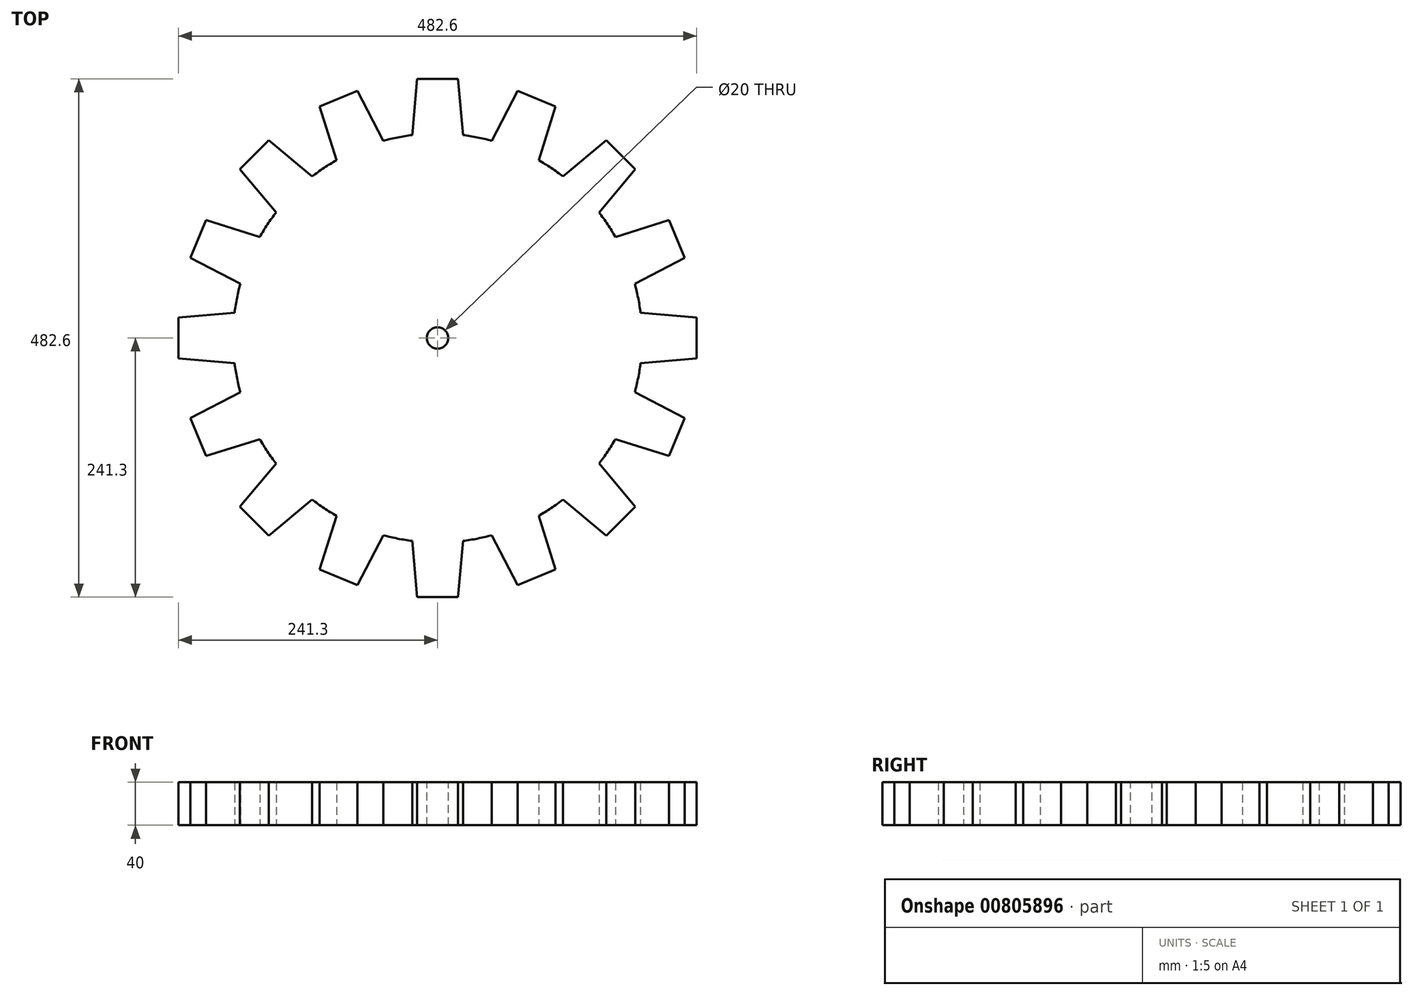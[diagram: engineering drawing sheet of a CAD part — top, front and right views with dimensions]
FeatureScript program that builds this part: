
annotation { "Feature Type Name" : "Feature", "Feature Type Description" : "" }
export const myFeature = defineFeature(function(context is Context, id is Id, definition is map)
    precondition{}
    {
        {
            var Q0;
            Q0=qCreatedBy(makeId("Top.planeOp"),FACE);
            var sketch = newSketch(context, id + "F0", { "sketchPlane" : qUnion([Q0])});
            skCircle(sketch, "E0", {"center": v(0, 0) * mm, "radius": 190.5 * mm});
            skLineSegment(sketch, "E1", {"start": v(0, 0) * mm, "end": v(0, 190.5) * mm, "construction": true});
            skLineSegment(sketch, "E2", {"start": v(-23.62, 189.03) * mm, "end": v(-19.05, 241.3) * mm});
            skLineSegment(sketch, "E3", {"start": v(-19.05, 241.3) * mm, "end": v(0, 241.3) * mm});
            skLineSegment(sketch, "E4.MirrorCS", {"start": v(23.62, 189.03) * mm, "end": v(19.05, 241.3) * mm});
            skLineSegment(sketch, "E5.MirrorCS", {"start": v(19.05, 241.3) * mm, "end": v(0, 241.3) * mm});
            skLineSegment(sketch, "E6.1.0", {"start": v(-94.16, 165.6) * mm, "end": v(-109.94, 215.64) * mm});
            skLineSegment(sketch, "E6.1.1", {"start": v(-109.94, 215.64) * mm, "end": v(-92.34, 222.93) * mm});
            skLineSegment(sketch, "E6.1.2", {"start": v(-74.74, 230.22) * mm, "end": v(-92.34, 222.93) * mm});
            skLineSegment(sketch, "E6.1.3", {"start": v(-50.51, 183.68) * mm, "end": v(-74.74, 230.22) * mm});
            skLineSegment(sketch, "E6.2.0", {"start": v(-150.37, 116.96) * mm, "end": v(-184.1, 157.15) * mm});
            skLineSegment(sketch, "E6.2.1", {"start": v(-184.1, 157.15) * mm, "end": v(-170.62, 170.62) * mm});
            skLineSegment(sketch, "E6.2.2", {"start": v(-157.15, 184.1) * mm, "end": v(-170.62, 170.62) * mm});
            skLineSegment(sketch, "E6.2.3", {"start": v(-116.96, 150.37) * mm, "end": v(-157.15, 184.1) * mm});
            skLineSegment(sketch, "E6.3.0", {"start": v(-183.68, 50.51) * mm, "end": v(-230.22, 74.74) * mm});
            skLineSegment(sketch, "E6.3.1", {"start": v(-230.22, 74.74) * mm, "end": v(-222.93, 92.34) * mm});
            skLineSegment(sketch, "E6.3.2", {"start": v(-215.64, 109.94) * mm, "end": v(-222.93, 92.34) * mm});
            skLineSegment(sketch, "E6.3.3", {"start": v(-165.6, 94.16) * mm, "end": v(-215.64, 109.94) * mm});
            skLineSegment(sketch, "E6.4.0", {"start": v(-189.03, -23.62) * mm, "end": v(-241.3, -19.05) * mm});
            skLineSegment(sketch, "E6.4.1", {"start": v(-241.3, -19.05) * mm, "end": v(-241.3, 0) * mm});
            skLineSegment(sketch, "E6.4.2", {"start": v(-241.3, 19.05) * mm, "end": v(-241.3, 0) * mm});
            skLineSegment(sketch, "E6.4.3", {"start": v(-189.03, 23.62) * mm, "end": v(-241.3, 19.05) * mm});
            skLineSegment(sketch, "E6.5.0", {"start": v(-165.6, -94.16) * mm, "end": v(-215.64, -109.94) * mm});
            skLineSegment(sketch, "E6.5.1", {"start": v(-215.64, -109.94) * mm, "end": v(-222.93, -92.34) * mm});
            skLineSegment(sketch, "E6.5.2", {"start": v(-230.22, -74.74) * mm, "end": v(-222.93, -92.34) * mm});
            skLineSegment(sketch, "E6.5.3", {"start": v(-183.68, -50.51) * mm, "end": v(-230.22, -74.74) * mm});
            skLineSegment(sketch, "E6.6.0", {"start": v(-116.96, -150.37) * mm, "end": v(-157.15, -184.1) * mm});
            skLineSegment(sketch, "E6.6.1", {"start": v(-157.15, -184.1) * mm, "end": v(-170.62, -170.62) * mm});
            skLineSegment(sketch, "E6.6.2", {"start": v(-184.1, -157.15) * mm, "end": v(-170.62, -170.62) * mm});
            skLineSegment(sketch, "E6.6.3", {"start": v(-150.37, -116.96) * mm, "end": v(-184.1, -157.15) * mm});
            skLineSegment(sketch, "E6.7.0", {"start": v(-50.51, -183.68) * mm, "end": v(-74.74, -230.22) * mm});
            skLineSegment(sketch, "E6.7.1", {"start": v(-74.74, -230.22) * mm, "end": v(-92.34, -222.93) * mm});
            skLineSegment(sketch, "E6.7.2", {"start": v(-109.94, -215.64) * mm, "end": v(-92.34, -222.93) * mm});
            skLineSegment(sketch, "E6.7.3", {"start": v(-94.16, -165.6) * mm, "end": v(-109.94, -215.64) * mm});
            skLineSegment(sketch, "E6.8.0", {"start": v(23.62, -189.03) * mm, "end": v(19.05, -241.3) * mm});
            skLineSegment(sketch, "E6.8.1", {"start": v(19.05, -241.3) * mm, "end": v(0, -241.3) * mm});
            skLineSegment(sketch, "E6.8.2", {"start": v(-19.05, -241.3) * mm, "end": v(0, -241.3) * mm});
            skLineSegment(sketch, "E6.8.3", {"start": v(-23.62, -189.03) * mm, "end": v(-19.05, -241.3) * mm});
            skLineSegment(sketch, "E6.9.0", {"start": v(94.16, -165.6) * mm, "end": v(109.94, -215.64) * mm});
            skLineSegment(sketch, "E6.9.1", {"start": v(109.94, -215.64) * mm, "end": v(92.34, -222.93) * mm});
            skLineSegment(sketch, "E6.9.2", {"start": v(74.74, -230.22) * mm, "end": v(92.34, -222.93) * mm});
            skLineSegment(sketch, "E6.9.3", {"start": v(50.51, -183.68) * mm, "end": v(74.74, -230.22) * mm});
            skLineSegment(sketch, "E6.10.0", {"start": v(150.37, -116.96) * mm, "end": v(184.1, -157.15) * mm});
            skLineSegment(sketch, "E6.10.1", {"start": v(184.1, -157.15) * mm, "end": v(170.62, -170.62) * mm});
            skLineSegment(sketch, "E6.10.2", {"start": v(157.15, -184.1) * mm, "end": v(170.62, -170.62) * mm});
            skLineSegment(sketch, "E6.10.3", {"start": v(116.96, -150.37) * mm, "end": v(157.15, -184.1) * mm});
            skLineSegment(sketch, "E6.11.0", {"start": v(183.68, -50.51) * mm, "end": v(230.22, -74.74) * mm});
            skLineSegment(sketch, "E6.11.1", {"start": v(230.22, -74.74) * mm, "end": v(222.93, -92.34) * mm});
            skLineSegment(sketch, "E6.11.2", {"start": v(215.64, -109.94) * mm, "end": v(222.93, -92.34) * mm});
            skLineSegment(sketch, "E6.11.3", {"start": v(165.6, -94.16) * mm, "end": v(215.64, -109.94) * mm});
            skLineSegment(sketch, "E6.12.0", {"start": v(189.03, 23.62) * mm, "end": v(241.3, 19.05) * mm});
            skLineSegment(sketch, "E6.12.1", {"start": v(241.3, 19.05) * mm, "end": v(241.3, 0) * mm});
            skLineSegment(sketch, "E6.12.2", {"start": v(241.3, -19.05) * mm, "end": v(241.3, 0) * mm});
            skLineSegment(sketch, "E6.12.3", {"start": v(189.03, -23.62) * mm, "end": v(241.3, -19.05) * mm});
            skLineSegment(sketch, "E6.13.0", {"start": v(165.6, 94.16) * mm, "end": v(215.64, 109.94) * mm});
            skLineSegment(sketch, "E6.13.1", {"start": v(215.64, 109.94) * mm, "end": v(222.93, 92.34) * mm});
            skLineSegment(sketch, "E6.13.2", {"start": v(230.22, 74.74) * mm, "end": v(222.93, 92.34) * mm});
            skLineSegment(sketch, "E6.13.3", {"start": v(183.68, 50.51) * mm, "end": v(230.22, 74.74) * mm});
            skLineSegment(sketch, "E6.14.0", {"start": v(116.96, 150.37) * mm, "end": v(157.15, 184.1) * mm});
            skLineSegment(sketch, "E6.14.1", {"start": v(157.15, 184.1) * mm, "end": v(170.62, 170.62) * mm});
            skLineSegment(sketch, "E6.14.2", {"start": v(184.1, 157.15) * mm, "end": v(170.62, 170.62) * mm});
            skLineSegment(sketch, "E6.14.3", {"start": v(150.37, 116.96) * mm, "end": v(184.1, 157.15) * mm});
            skLineSegment(sketch, "E6.15.0", {"start": v(50.51, 183.68) * mm, "end": v(74.74, 230.22) * mm});
            skLineSegment(sketch, "E6.15.1", {"start": v(74.74, 230.22) * mm, "end": v(92.34, 222.93) * mm});
            skLineSegment(sketch, "E6.15.2", {"start": v(109.94, 215.64) * mm, "end": v(92.34, 222.93) * mm});
            skLineSegment(sketch, "E6.15.3", {"start": v(94.16, 165.6) * mm, "end": v(109.94, 215.64) * mm});
            skSolve(sketch);
        }
        {
            var Q0;
            {var subQ0=sQuery(id+"F0.wireOp",EDGE,"E0");var subQ18=makeQuery(id+"F0.imprint","INTERSECT",VERTEX,{"derivedFrom":[subQ0,sQuery(id+"F0.wireOp",EDGE,"E6.12.0")]});Q0=makeQuery(id+"F0.imprint","IMPRINT",FACE,{"disambiguationData":[TD([[makeQuery(id+"F0.imprint","IMPRINT",EDGE,{"disambiguationData":[TD([[subQ18,-1.0]])],"derivedFrom":subQ0}),1.0]])]});}
            var Q1;
            Q1=qSketchRegion(id+"F0",true);
            extrude(context, id + "F1", {"entities" : qUnion([Q0, Q1]), "depth" : 20 * mm, "offsetDistance" : 25.4 * mm});
        }
        {
            var Q0;
            Q0=makeQuery(id+"F1.opExtrude","CAP_FACE",FACE,{"disambiguationData":[OSD([sQuery(id+"F0.wireOp",EDGE,"E0"),sQuery(id+"F0.wireOp",EDGE,"E2"),sQuery(id+"F0.wireOp",EDGE,"E3"),sQuery(id+"F0.wireOp",EDGE,"E4.MirrorCS"),sQuery(id+"F0.wireOp",EDGE,"E5.MirrorCS"),sQuery(id+"F0.wireOp",EDGE,"E6.1.0"),sQuery(id+"F0.wireOp",EDGE,"E6.1.1"),sQuery(id+"F0.wireOp",EDGE,"E6.1.2"),sQuery(id+"F0.wireOp",EDGE,"E6.1.3"),sQuery(id+"F0.wireOp",EDGE,"E6.2.0"),sQuery(id+"F0.wireOp",EDGE,"E6.2.1"),sQuery(id+"F0.wireOp",EDGE,"E6.2.2"),sQuery(id+"F0.wireOp",EDGE,"E6.2.3"),sQuery(id+"F0.wireOp",EDGE,"E6.3.0"),sQuery(id+"F0.wireOp",EDGE,"E6.3.1"),sQuery(id+"F0.wireOp",EDGE,"E6.3.2"),sQuery(id+"F0.wireOp",EDGE,"E6.3.3"),sQuery(id+"F0.wireOp",EDGE,"E6.4.0"),sQuery(id+"F0.wireOp",EDGE,"E6.4.1"),sQuery(id+"F0.wireOp",EDGE,"E6.4.2"),sQuery(id+"F0.wireOp",EDGE,"E6.4.3"),sQuery(id+"F0.wireOp",EDGE,"E6.5.0"),sQuery(id+"F0.wireOp",EDGE,"E6.5.1"),sQuery(id+"F0.wireOp",EDGE,"E6.5.2"),sQuery(id+"F0.wireOp",EDGE,"E6.5.3"),sQuery(id+"F0.wireOp",EDGE,"E6.6.0"),sQuery(id+"F0.wireOp",EDGE,"E6.6.1"),sQuery(id+"F0.wireOp",EDGE,"E6.6.2"),sQuery(id+"F0.wireOp",EDGE,"E6.6.3"),sQuery(id+"F0.wireOp",EDGE,"E6.7.0"),sQuery(id+"F0.wireOp",EDGE,"E6.7.1"),sQuery(id+"F0.wireOp",EDGE,"E6.7.2"),sQuery(id+"F0.wireOp",EDGE,"E6.7.3"),sQuery(id+"F0.wireOp",EDGE,"E6.8.0"),sQuery(id+"F0.wireOp",EDGE,"E6.8.1"),sQuery(id+"F0.wireOp",EDGE,"E6.8.2"),sQuery(id+"F0.wireOp",EDGE,"E6.8.3"),sQuery(id+"F0.wireOp",EDGE,"E6.9.0"),sQuery(id+"F0.wireOp",EDGE,"E6.9.1"),sQuery(id+"F0.wireOp",EDGE,"E6.9.2"),sQuery(id+"F0.wireOp",EDGE,"E6.9.3"),sQuery(id+"F0.wireOp",EDGE,"E6.10.0"),sQuery(id+"F0.wireOp",EDGE,"E6.10.1"),sQuery(id+"F0.wireOp",EDGE,"E6.10.2"),sQuery(id+"F0.wireOp",EDGE,"E6.10.3"),sQuery(id+"F0.wireOp",EDGE,"E6.11.0"),sQuery(id+"F0.wireOp",EDGE,"E6.11.1"),sQuery(id+"F0.wireOp",EDGE,"E6.11.2"),sQuery(id+"F0.wireOp",EDGE,"E6.11.3"),sQuery(id+"F0.wireOp",EDGE,"E6.12.0"),sQuery(id+"F0.wireOp",EDGE,"E6.12.1"),sQuery(id+"F0.wireOp",EDGE,"E6.12.2"),sQuery(id+"F0.wireOp",EDGE,"E6.12.3"),sQuery(id+"F0.wireOp",EDGE,"E6.13.0"),sQuery(id+"F0.wireOp",EDGE,"E6.13.1"),sQuery(id+"F0.wireOp",EDGE,"E6.13.2"),sQuery(id+"F0.wireOp",EDGE,"E6.13.3"),sQuery(id+"F0.wireOp",EDGE,"E6.14.0"),sQuery(id+"F0.wireOp",EDGE,"E6.14.1"),sQuery(id+"F0.wireOp",EDGE,"E6.14.2"),sQuery(id+"F0.wireOp",EDGE,"E6.14.3"),sQuery(id+"F0.wireOp",EDGE,"E6.15.0"),sQuery(id+"F0.wireOp",EDGE,"E6.15.1"),sQuery(id+"F0.wireOp",EDGE,"E6.15.2"),sQuery(id+"F0.wireOp",EDGE,"E6.15.3")])],"isStart":false});
            var sketch = newSketch(context, id + "F2", { "sketchPlane" : qUnion([Q0])});
            skCircle(sketch, "E7", {"center": v(0, 0) * mm, "radius": 10 * mm});
            skSolve(sketch);
        }
        {
            var Q0;
            Q0=qSketchRegion(id+"F2",true);
            extrude(context, id + "F3", {"entities" : qUnion([Q0]), "operationType" : NewBodyOperationType.REMOVE, "endBound" : BoundingType.THROUGH_ALL, "oppositeDirection" : true, "depth" : 25 * mm, "offsetDistance" : 25 * mm});
        }
        {
            var Q0;
            Q0=makeQuery(id+"F1.opExtrude","CAP_FACE",FACE,{"disambiguationData":[OSD([sQuery(id+"F0.wireOp",EDGE,"E0"),sQuery(id+"F0.wireOp",EDGE,"E2"),sQuery(id+"F0.wireOp",EDGE,"E3"),sQuery(id+"F0.wireOp",EDGE,"E4.MirrorCS"),sQuery(id+"F0.wireOp",EDGE,"E5.MirrorCS"),sQuery(id+"F0.wireOp",EDGE,"E6.1.0"),sQuery(id+"F0.wireOp",EDGE,"E6.1.1"),sQuery(id+"F0.wireOp",EDGE,"E6.1.2"),sQuery(id+"F0.wireOp",EDGE,"E6.1.3"),sQuery(id+"F0.wireOp",EDGE,"E6.2.0"),sQuery(id+"F0.wireOp",EDGE,"E6.2.1"),sQuery(id+"F0.wireOp",EDGE,"E6.2.2"),sQuery(id+"F0.wireOp",EDGE,"E6.2.3"),sQuery(id+"F0.wireOp",EDGE,"E6.3.0"),sQuery(id+"F0.wireOp",EDGE,"E6.3.1"),sQuery(id+"F0.wireOp",EDGE,"E6.3.2"),sQuery(id+"F0.wireOp",EDGE,"E6.3.3"),sQuery(id+"F0.wireOp",EDGE,"E6.4.0"),sQuery(id+"F0.wireOp",EDGE,"E6.4.1"),sQuery(id+"F0.wireOp",EDGE,"E6.4.2"),sQuery(id+"F0.wireOp",EDGE,"E6.4.3"),sQuery(id+"F0.wireOp",EDGE,"E6.5.0"),sQuery(id+"F0.wireOp",EDGE,"E6.5.1"),sQuery(id+"F0.wireOp",EDGE,"E6.5.2"),sQuery(id+"F0.wireOp",EDGE,"E6.5.3"),sQuery(id+"F0.wireOp",EDGE,"E6.6.0"),sQuery(id+"F0.wireOp",EDGE,"E6.6.1"),sQuery(id+"F0.wireOp",EDGE,"E6.6.2"),sQuery(id+"F0.wireOp",EDGE,"E6.6.3"),sQuery(id+"F0.wireOp",EDGE,"E6.7.0"),sQuery(id+"F0.wireOp",EDGE,"E6.7.1"),sQuery(id+"F0.wireOp",EDGE,"E6.7.2"),sQuery(id+"F0.wireOp",EDGE,"E6.7.3"),sQuery(id+"F0.wireOp",EDGE,"E6.8.0"),sQuery(id+"F0.wireOp",EDGE,"E6.8.1"),sQuery(id+"F0.wireOp",EDGE,"E6.8.2"),sQuery(id+"F0.wireOp",EDGE,"E6.8.3"),sQuery(id+"F0.wireOp",EDGE,"E6.9.0"),sQuery(id+"F0.wireOp",EDGE,"E6.9.1"),sQuery(id+"F0.wireOp",EDGE,"E6.9.2"),sQuery(id+"F0.wireOp",EDGE,"E6.9.3"),sQuery(id+"F0.wireOp",EDGE,"E6.10.0"),sQuery(id+"F0.wireOp",EDGE,"E6.10.1"),sQuery(id+"F0.wireOp",EDGE,"E6.10.2"),sQuery(id+"F0.wireOp",EDGE,"E6.10.3"),sQuery(id+"F0.wireOp",EDGE,"E6.11.0"),sQuery(id+"F0.wireOp",EDGE,"E6.11.1"),sQuery(id+"F0.wireOp",EDGE,"E6.11.2"),sQuery(id+"F0.wireOp",EDGE,"E6.11.3"),sQuery(id+"F0.wireOp",EDGE,"E6.12.0"),sQuery(id+"F0.wireOp",EDGE,"E6.12.1"),sQuery(id+"F0.wireOp",EDGE,"E6.12.2"),sQuery(id+"F0.wireOp",EDGE,"E6.12.3"),sQuery(id+"F0.wireOp",EDGE,"E6.13.0"),sQuery(id+"F0.wireOp",EDGE,"E6.13.1"),sQuery(id+"F0.wireOp",EDGE,"E6.13.2"),sQuery(id+"F0.wireOp",EDGE,"E6.13.3"),sQuery(id+"F0.wireOp",EDGE,"E6.14.0"),sQuery(id+"F0.wireOp",EDGE,"E6.14.1"),sQuery(id+"F0.wireOp",EDGE,"E6.14.2"),sQuery(id+"F0.wireOp",EDGE,"E6.14.3"),sQuery(id+"F0.wireOp",EDGE,"E6.15.0"),sQuery(id+"F0.wireOp",EDGE,"E6.15.1"),sQuery(id+"F0.wireOp",EDGE,"E6.15.2"),sQuery(id+"F0.wireOp",EDGE,"E6.15.3")])],"isStart":false});
            extrude(context, id + "F4", {"entities" : qUnion([Q0]), "operationType" : NewBodyOperationType.ADD, "depth" : 20 * mm, "offsetDistance" : 25 * mm});
        }
    });
